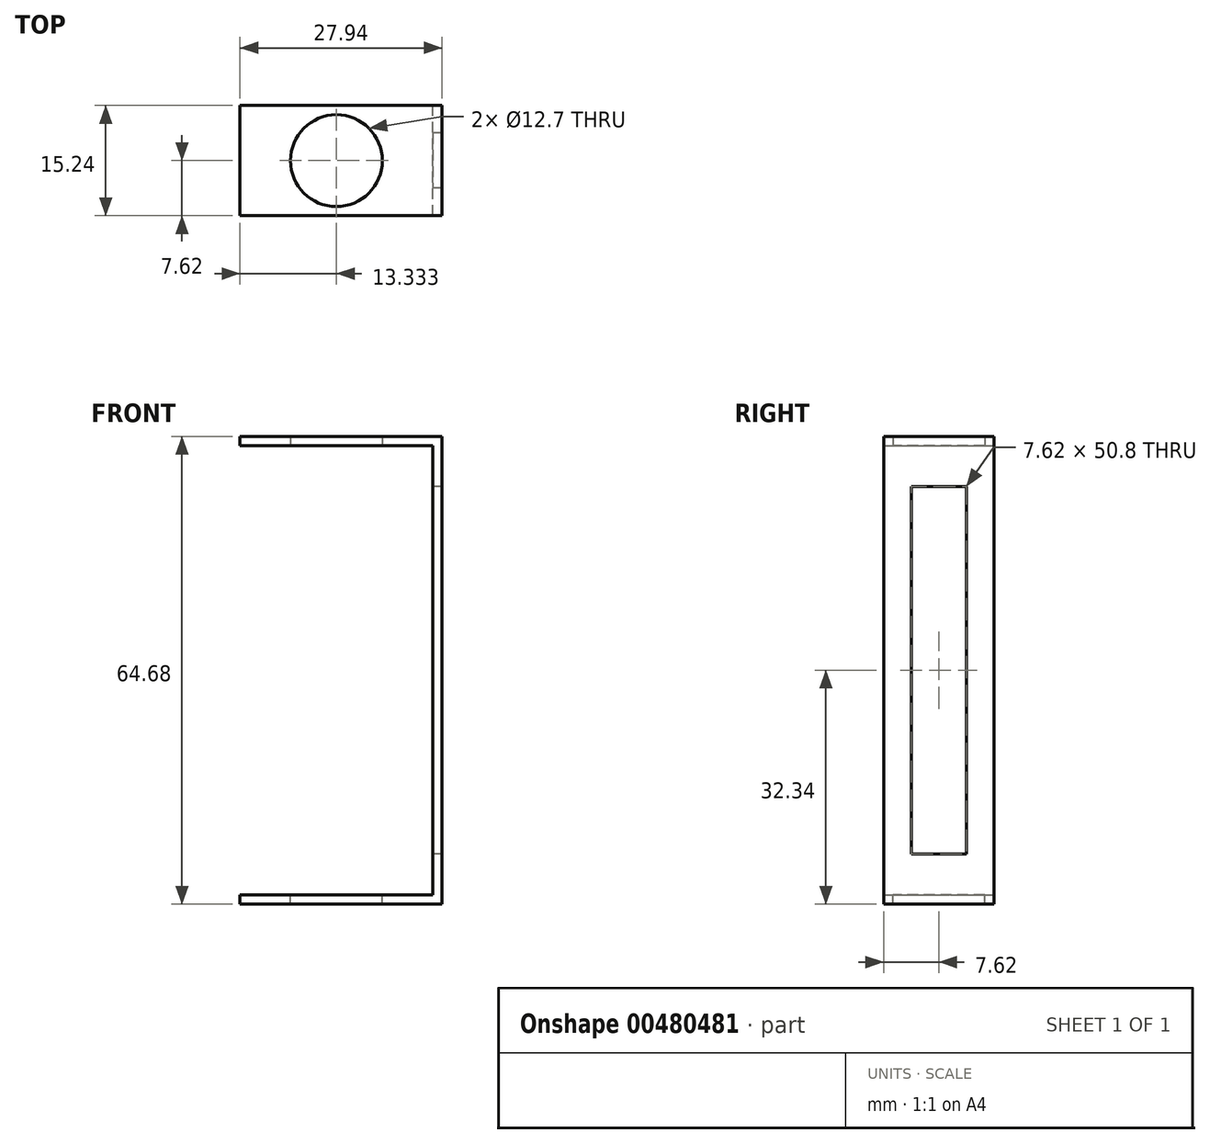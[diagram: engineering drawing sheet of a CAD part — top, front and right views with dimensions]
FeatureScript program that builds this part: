
annotation { "Feature Type Name" : "Feature", "Feature Type Description" : "" }
export const myFeature = defineFeature(function(context is Context, id is Id, definition is map)
    precondition{}
    {
        {
            var Q0;
            Q0=qCreatedBy(makeId("Front.planeOp"),FACE);
            var sketch = newSketch(context, id + "F0", { "sketchPlane" : qUnion([Q0])});
            skLineSegment(sketch, "E0", {"start": v(13.47, -37.18) * mm, "end": v(13.47, 27.5) * mm});
            skLineSegment(sketch, "E1", {"start": v(13.47, 27.5) * mm, "end": v(-14.47, 27.5) * mm});
            skLineSegment(sketch, "E2", {"start": v(13.47, -37.18) * mm, "end": v(-14.47, -37.18) * mm});
            skPoint(sketch, "E3.end.orphan", {"position": v(-22.75, 44.3) * mm});
            skPoint(sketch, "E4.end.orphan", {"position": v(-13.23, 29.8) * mm});
            skLineSegment(sketch, "E5", {"start": v(-14.47, -37.18) * mm, "end": v(-14.47, -35.91) * mm});
            skLineSegment(sketch, "E6", {"start": v(-14.47, -35.91) * mm, "end": v(12.2, -35.91) * mm});
            skLineSegment(sketch, "E7", {"start": v(12.2, -35.91) * mm, "end": v(12.2, 26.23) * mm});
            skLineSegment(sketch, "E8", {"start": v(12.2, 26.23) * mm, "end": v(-14.47, 26.23) * mm});
            skLineSegment(sketch, "E9", {"start": v(-14.47, 27.5) * mm, "end": v(-14.47, 26.23) * mm});
            skSolve(sketch);
        }
        {
            var Q0;
            Q0=makeQuery(id+"F0.imprint","IMPRINT",FACE,{"disambiguationData":[TD([[makeQuery(id+"F0.imprint","IMPRINT",EDGE,{"derivedFrom":sQuery(id+"F0.wireOp",EDGE,"E0")}),1.0]])]});
            extrude(context, id + "F1", {"entities" : qUnion([Q0]), "depth" : 15.24 * mm});
        }
        {
            var Q0;
            Q0=makeQuery(id+"F1.opExtrude","SWEPT_FACE",FACE,{"disambiguationData":[OSD([sQuery(id+"F0.wireOp",EDGE,"E8")])]});
            var sketch = newSketch(context, id + "F2", { "sketchPlane" : qUnion([Q0])});
            skLineSegment(sketch, "E10", {"start": v(12.2, 15.24) * mm, "end": v(12.2, 15.24) * mm});
            skPoint(sketch, "E11.orphan", {"position": v(12.2, 0) * mm});
            skLineSegment(sketch, "E12", {"start": v(-14.47, 15.24) * mm, "end": v(-14.47, 0) * mm});
            skLineSegment(sketch, "E13", {"start": v(-14.47, 0) * mm, "end": v(-14.47, 7.62) * mm});
            skLineSegment(sketch, "E14", {"start": v(-6.22, 7.62) * mm, "end": v(-1.14, 7.62) * mm});
            skCircle(sketch, "E15", {"center": v(-1.14, 7.62) * mm, "radius": 5.08 * mm});
            skSolve(sketch);
        }
        {
            var Q0;
            Q0=makeQuery(id+"F1.opExtrude","SWEPT_FACE",FACE,{"disambiguationData":[OSD([sQuery(id+"F0.wireOp",EDGE,"E6")])]});
            var sketch = newSketch(context, id + "F3", { "sketchPlane" : qUnion([Q0])});
            skLineSegment(sketch, "E16", {"start": v(-14.47, 0) * mm, "end": v(-14.47, -15.24) * mm});
            skCircle(sketch, "E17", {"center": v(-1.14, -7.62) * mm, "radius": 5.08 * mm});
            skPoint(sketch, "E18.orphan", {"position": v(12.2, -15.24) * mm});
            skSolve(sketch);
        }
        {
            var Q0;
            Q0=sQuery(id+"F3.wireOp",VERTEX,"E17.center");
            var Q1;
            Q1=sQuery(id+"F2.wireOp",VERTEX,"gve0yRoe-hpo7-PdOA-Ka6Q-LxEZMsg8H7QF.center");
            var Q2;
            Q2=sQuery(id+"F2.wireOp",VERTEX,"E14.end");
            var Q3;
            Q3=makeQuery(id+"F1.opExtrude","SWEPT_BODY",BODY,{"disambiguationData":[OSD([sQuery(id+"F0.wireOp",EDGE,"E0"),sQuery(id+"F0.wireOp",EDGE,"E1"),sQuery(id+"F0.wireOp",EDGE,"E2"),sQuery(id+"F0.wireOp",EDGE,"VlnuhpvV-yOnj-QCpl-qx8X-MRNi2WwVTH3J"),sQuery(id+"F0.wireOp",EDGE,"E5"),sQuery(id+"F0.wireOp",EDGE,"E6"),sQuery(id+"F0.wireOp",EDGE,"E7"),sQuery(id+"F0.wireOp",EDGE,"E8"),sQuery(id+"F0.wireOp",EDGE,"X2vaGqFh-gO5O-PfaP-HTgo-mBHdgZOOPoy0"),sQuery(id+"F0.wireOp",EDGE,"94RsUK6E-MieE-cqY5-qvLV-zptDYSzb3KeZ")])]});
            hole(context, id + "F4", {"style" : HoleStyle.SIMPLE, "endStyle" : HoleEndStyle.THROUGH, "holeDiameter" : 12.7 * mm, "isTappedThrough" : true, "tappedDepth" : 12.7 * mm, "tapClearance" : 3, "locations" : qUnion([Q0, Q1, Q2]), "scope" : qUnion([Q3])});
        }
        {
            var Q0;
            Q0=makeQuery(id+"F1.opExtrude","SWEPT_FACE",FACE,{"disambiguationData":[OSD([sQuery(id+"F0.wireOp",EDGE,"E7")])]});
            var sketch = newSketch(context, id + "F5", { "sketchPlane" : qUnion([Q0])});
            skLineSegment(sketch, "E19", {"start": v(15.24, -4.84) * mm, "end": v(0, -4.84) * mm});
            skLineSegment(sketch, "E20.bottom", {"start": v(3.81, -30.24) * mm, "end": v(11.43, -30.24) * mm});
            skLineSegment(sketch, "E20.top", {"start": v(3.81, 20.56) * mm, "end": v(11.43, 20.56) * mm});
            skLineSegment(sketch, "E20.left", {"start": v(3.81, -30.24) * mm, "end": v(3.81, 20.56) * mm});
            skLineSegment(sketch, "E20.right", {"start": v(11.43, -30.24) * mm, "end": v(11.43, 20.56) * mm});
            skPoint(sketch, "E20.middle", {"position": v(7.62, -4.84) * mm});
            skSolve(sketch);
        }
        {
            var Q0;
            {var subQ5=sQuery(id+"F5.wireOp",EDGE,"E20.bottom");Q0=makeQuery(id+"F5.imprint","IMPRINT",FACE,{"disambiguationData":[TD([[makeQuery(id+"F5.imprint","IMPRINT",EDGE,{"derivedFrom":subQ5}),1.0]])]});}
            var Q1;
            {var subQ5=sQuery(id+"F5.wireOp",EDGE,"E20.top");Q1=makeQuery(id+"F5.imprint","IMPRINT",FACE,{"disambiguationData":[TD([[makeQuery(id+"F5.imprint","IMPRINT",EDGE,{"derivedFrom":subQ5}),-1.0]])]});}
            extrude(context, id + "F6", {"entities" : qUnion([Q0, Q1]), "operationType" : NewBodyOperationType.REMOVE, "oppositeDirection" : true, "depth" : 25.4 * mm});
        }
    });
